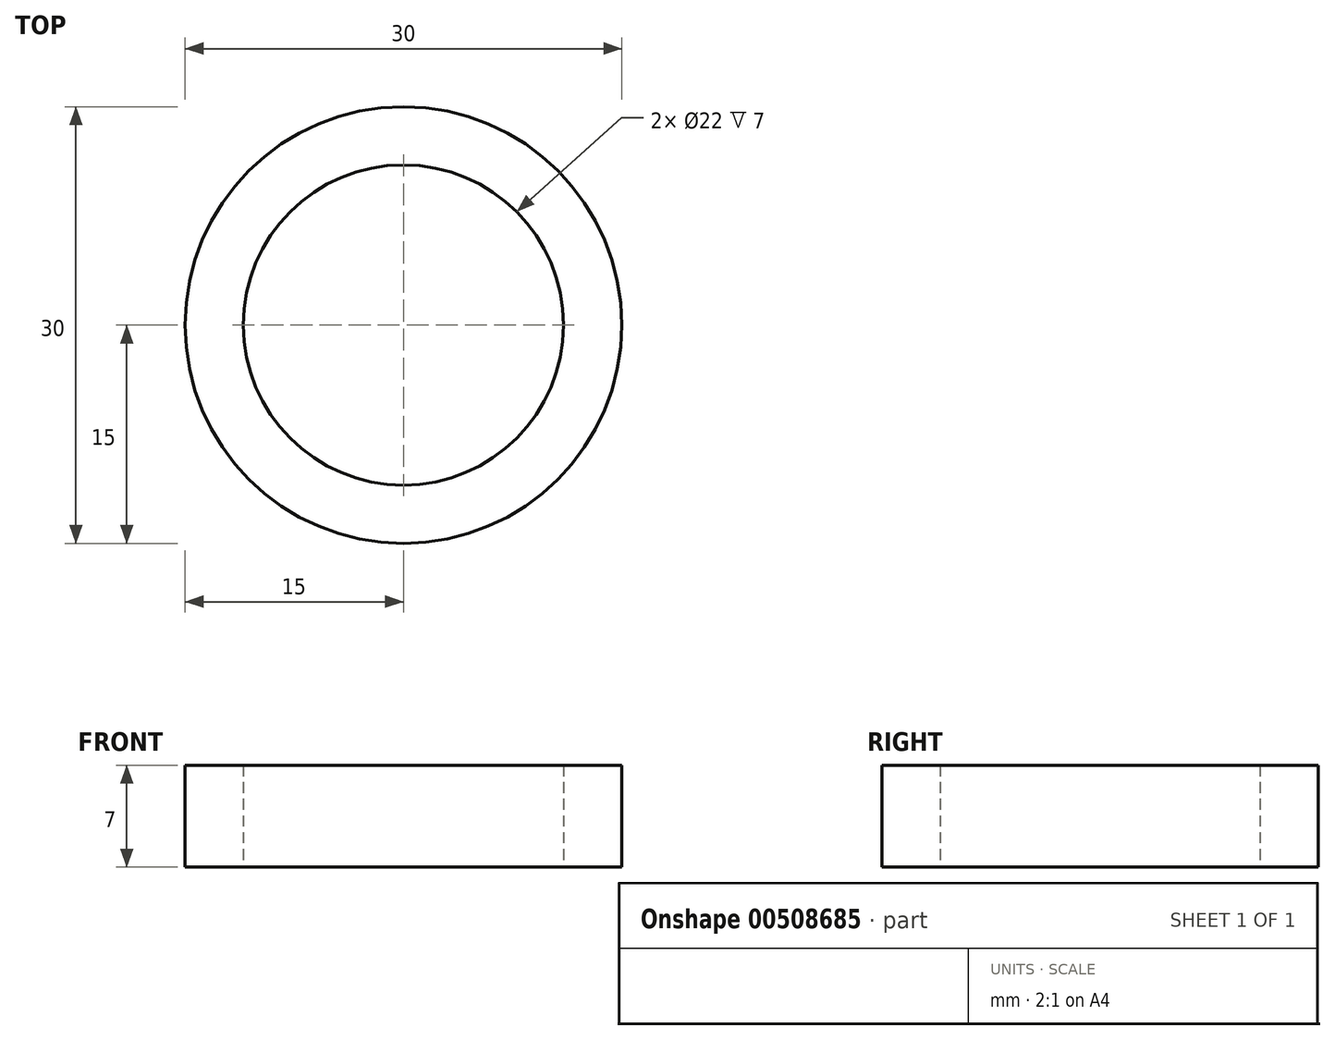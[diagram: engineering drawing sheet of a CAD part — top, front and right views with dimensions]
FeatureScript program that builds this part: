
annotation { "Feature Type Name" : "Feature", "Feature Type Description" : "" }
export const myFeature = defineFeature(function(context is Context, id is Id, definition is map)
    precondition{}
    {
        {
            var Q0;
            Q0=qCreatedBy(makeId("Top.planeOp"),FACE);
            var sketch = newSketch(context, id + "F0", { "sketchPlane" : qUnion([Q0])});
            skCircle(sketch, "E0", {"center": v(0, 0) * mm, "radius": 15 * mm});
            skCircle(sketch, "E1", {"center": v(0, 0) * mm, "radius": 11 * mm});
            skSolve(sketch);
        }
        {
            var Q0;
            Q0 = qSketchRegion(id + "F0", true);
            extrude(context, id + "F1", {"entities" : qUnion([Q0]), "depth" : 7 * mm});
        }
    });
